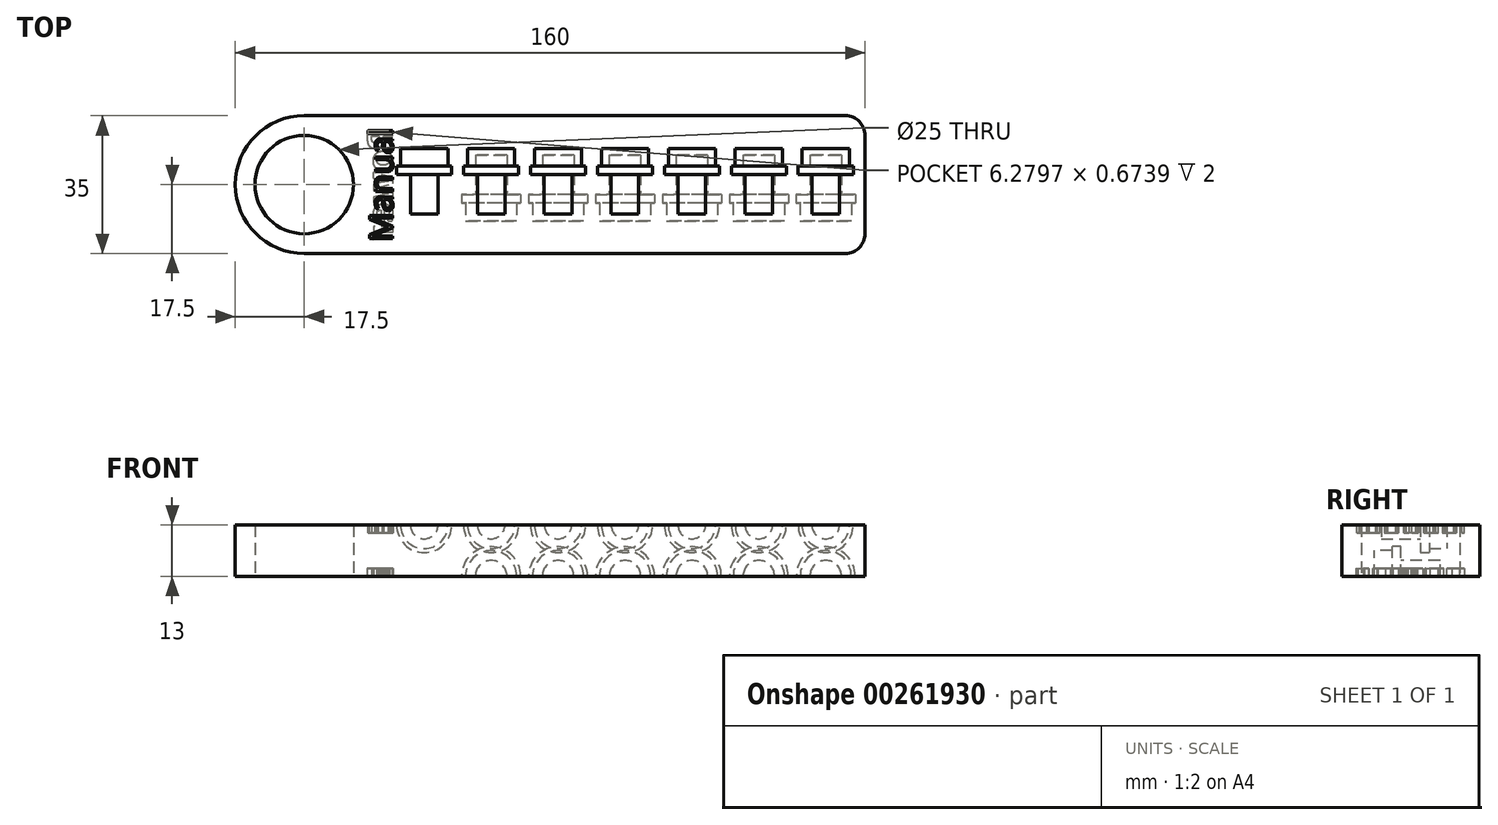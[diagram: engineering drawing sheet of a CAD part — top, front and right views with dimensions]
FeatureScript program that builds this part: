
annotation { "Feature Type Name" : "Feature", "Feature Type Description" : "" }
export const myFeature = defineFeature(function(context is Context, id is Id, definition is map)
    precondition{}
    {
        {
            var Q0;
            Q0=qCreatedBy(makeId("Top.planeOp"),FACE);
            var sketch = newSketch(context, id + "F0", { "sketchPlane" : qUnion([Q0])});
            skLineSegment(sketch, "E0.bottom", {"start": v(17.5, 0) * mm, "end": v(155, 0) * mm});
            skLineSegment(sketch, "E0.top", {"start": v(17.5, 35) * mm, "end": v(155, 35) * mm});
            skLineSegment(sketch, "E0.left", {"start": v(0, 17.5) * mm, "end": v(0, 17.5) * mm});
            skLineSegment(sketch, "E0.right", {"start": v(160, 5) * mm, "end": v(160, 30) * mm});
            skLineSegment(sketch, "E1.bottom", {"start": v(0, 0) * mm, "end": v(17.5, 0) * mm, "construction": true});
            skLineSegment(sketch, "E1.top", {"start": v(0, 17.5) * mm, "end": v(17.5, 17.5) * mm, "construction": true});
            skLineSegment(sketch, "E1.left", {"start": v(0, 0) * mm, "end": v(0, 17.5) * mm, "construction": true});
            skLineSegment(sketch, "E1.right", {"start": v(17.5, 0) * mm, "end": v(17.5, 17.5) * mm, "construction": true});
            skCircle(sketch, "E2", {"center": v(17.5, 17.5) * mm, "radius": 12.5 * mm});
            skPoint(sketch, "E3.visualSharp", {"position": v(0, 35) * mm});
            skArc(sketch, "E3.filletArc", {"start": v(17.5, 35) * mm, "mid": v(5.13, 29.87) * mm, "end": v(0, 17.5) * mm});
            skPoint(sketch, "E4.visualSharp", {"position": v(0, 0) * mm});
            skArc(sketch, "E4.filletArc", {"start": v(0, 17.5) * mm, "mid": v(5.13, 5.13) * mm, "end": v(17.5, 0) * mm});
            skPoint(sketch, "E5.visualSharp", {"position": v(160, 35) * mm});
            skArc(sketch, "E5.filletArc", {"start": v(160, 30) * mm, "mid": v(158.54, 33.54) * mm, "end": v(155, 35) * mm});
            skPoint(sketch, "E6.visualSharp", {"position": v(160, 0) * mm});
            skArc(sketch, "E6.filletArc", {"start": v(155, 0) * mm, "mid": v(158.54, 1.46) * mm, "end": v(160, 5) * mm});
            skSolve(sketch);
        }
        {
            var Q0;
            Q0=makeQuery(id+"F0.imprint","IMPRINT",FACE,{"disambiguationData":[TD([[makeQuery(id+"F0.imprint","IMPRINT",EDGE,{"derivedFrom":sQuery(id+"F0.wireOp",EDGE,"E0.bottom")}),1.0]])]});
            extrude(context, id + "F1", {"entities" : qUnion([Q0]), "depth" : 13 * mm});
        }
        {
            var Q0;
            Q0=makeQuery(id+"F1.opExtrude","CAP_FACE",FACE,{"disambiguationData":[OSD([sQuery(id+"F0.wireOp",EDGE,"E0.bottom"),sQuery(id+"F0.wireOp",EDGE,"E0.top"),sQuery(id+"F0.wireOp",EDGE,"E0.left"),sQuery(id+"F0.wireOp",EDGE,"E0.right"),sQuery(id+"F0.wireOp",EDGE,"E2"),sQuery(id+"F0.wireOp",EDGE,"E3.filletArc"),sQuery(id+"F0.wireOp",EDGE,"E4.filletArc"),sQuery(id+"F0.wireOp",EDGE,"E5.filletArc"),sQuery(id+"F0.wireOp",EDGE,"E6.filletArc")])],"isStart":false});
            var sketch = newSketch(context, id + "F2", { "sketchPlane" : qUnion([Q0])});
            skLineSegment(sketch, "E7.bottom", {"start": v(0, 0) * mm, "end": v(48, 0) * mm, "construction": true});
            skLineSegment(sketch, "E7.top", {"start": v(0, 10) * mm, "end": v(48, 10) * mm, "construction": true});
            skLineSegment(sketch, "E7.left", {"start": v(0, 0) * mm, "end": v(0, 10) * mm, "construction": true});
            skLineSegment(sketch, "E7.right", {"start": v(48, 0) * mm, "end": v(48, 10) * mm, "construction": true});
            skLineSegment(sketch, "E8", {"start": v(48, 10) * mm, "end": v(65, 10) * mm, "construction": true});
            skLineSegment(sketch, "E9", {"start": v(65, 10) * mm, "end": v(82, 10) * mm, "construction": true});
            skLineSegment(sketch, "E10", {"start": v(82, 10) * mm, "end": v(99, 10) * mm, "construction": true});
            skLineSegment(sketch, "E11", {"start": v(99, 10) * mm, "end": v(116, 10) * mm, "construction": true});
            skLineSegment(sketch, "E12", {"start": v(116, 10) * mm, "end": v(133, 10) * mm, "construction": true});
            skLineSegment(sketch, "E13", {"start": v(133, 10) * mm, "end": v(150, 10) * mm, "construction": true});
            skLineSegment(sketch, "E14.bottom", {"start": v(48, 10) * mm, "end": v(51.5, 10) * mm});
            skLineSegment(sketch, "E14.left", {"start": v(48, 10) * mm, "end": v(48, 20) * mm});
            skLineSegment(sketch, "E14.right", {"start": v(51.5, 10) * mm, "end": v(51.5, 20) * mm});
            skLineSegment(sketch, "E15.bottom", {"start": v(65, 10) * mm, "end": v(68.5, 10) * mm});
            skLineSegment(sketch, "E15.left", {"start": v(65, 10) * mm, "end": v(65, 20) * mm});
            skLineSegment(sketch, "E15.right", {"start": v(68.5, 10) * mm, "end": v(68.5, 20) * mm});
            skLineSegment(sketch, "E16.bottom", {"start": v(82, 10) * mm, "end": v(85.5, 10) * mm});
            skLineSegment(sketch, "E16.left", {"start": v(82, 10) * mm, "end": v(82, 20) * mm});
            skLineSegment(sketch, "E16.right", {"start": v(85.5, 10) * mm, "end": v(85.5, 20) * mm});
            skLineSegment(sketch, "E17.bottom", {"start": v(99, 10) * mm, "end": v(102.5, 10) * mm});
            skLineSegment(sketch, "E17.left", {"start": v(99, 10) * mm, "end": v(99, 20) * mm});
            skLineSegment(sketch, "E17.right", {"start": v(102.5, 10) * mm, "end": v(102.5, 20) * mm});
            skLineSegment(sketch, "E18.bottom", {"start": v(116, 10) * mm, "end": v(119.5, 10) * mm});
            skLineSegment(sketch, "E18.left", {"start": v(116, 10) * mm, "end": v(116, 20) * mm});
            skLineSegment(sketch, "E18.right", {"start": v(119.5, 10) * mm, "end": v(119.5, 20) * mm});
            skLineSegment(sketch, "E19.bottom", {"start": v(133, 10) * mm, "end": v(136.5, 10) * mm});
            skLineSegment(sketch, "E19.left", {"start": v(133, 10) * mm, "end": v(133, 20) * mm});
            skLineSegment(sketch, "E19.right", {"start": v(136.5, 10) * mm, "end": v(136.5, 20) * mm});
            skLineSegment(sketch, "E20.bottom", {"start": v(150, 10) * mm, "end": v(153.5, 10) * mm});
            skLineSegment(sketch, "E20.left", {"start": v(150, 10) * mm, "end": v(150, 20) * mm});
            skLineSegment(sketch, "E20.right", {"start": v(153.5, 10) * mm, "end": v(153.5, 20) * mm});
            skLineSegment(sketch, "E21.bottom", {"start": v(153.5, 20) * mm, "end": v(157, 20) * mm});
            skLineSegment(sketch, "E21.top", {"start": v(156, 22.2) * mm, "end": v(157, 22.2) * mm});
            skLineSegment(sketch, "E21.left", {"start": v(150, 20) * mm, "end": v(150, 22.2) * mm});
            skLineSegment(sketch, "E21.right", {"start": v(157, 20) * mm, "end": v(157, 22.2) * mm});
            skLineSegment(sketch, "E22.bottom", {"start": v(136.5, 20) * mm, "end": v(140, 20) * mm});
            skLineSegment(sketch, "E22.top", {"start": v(139, 22.2) * mm, "end": v(140, 22.2) * mm});
            skLineSegment(sketch, "E22.left", {"start": v(133, 20) * mm, "end": v(133, 22.2) * mm});
            skLineSegment(sketch, "E22.right", {"start": v(140, 20) * mm, "end": v(140, 22.2) * mm});
            skLineSegment(sketch, "E23.bottom", {"start": v(119.5, 20) * mm, "end": v(123, 20) * mm});
            skLineSegment(sketch, "E23.top", {"start": v(122, 22.2) * mm, "end": v(123, 22.2) * mm});
            skLineSegment(sketch, "E23.left", {"start": v(116, 20) * mm, "end": v(116, 22.2) * mm});
            skLineSegment(sketch, "E23.right", {"start": v(123, 20) * mm, "end": v(123, 22.2) * mm});
            skLineSegment(sketch, "E24.bottom", {"start": v(102.5, 20) * mm, "end": v(106, 20) * mm});
            skLineSegment(sketch, "E24.top", {"start": v(105, 22.2) * mm, "end": v(106, 22.2) * mm});
            skLineSegment(sketch, "E24.left", {"start": v(99, 20) * mm, "end": v(99, 22.2) * mm});
            skLineSegment(sketch, "E24.right", {"start": v(106, 20) * mm, "end": v(106, 22.2) * mm});
            skLineSegment(sketch, "E25.bottom", {"start": v(85.5, 20) * mm, "end": v(89, 20) * mm});
            skLineSegment(sketch, "E25.top", {"start": v(88, 22.2) * mm, "end": v(89, 22.2) * mm});
            skLineSegment(sketch, "E25.left", {"start": v(82, 20) * mm, "end": v(82, 22.2) * mm});
            skLineSegment(sketch, "E25.right", {"start": v(89, 20) * mm, "end": v(89, 22.2) * mm});
            skLineSegment(sketch, "E26.bottom", {"start": v(68.5, 20) * mm, "end": v(72, 20) * mm});
            skLineSegment(sketch, "E26.top", {"start": v(71, 22.2) * mm, "end": v(72, 22.2) * mm});
            skLineSegment(sketch, "E26.left", {"start": v(65, 20) * mm, "end": v(65, 22.2) * mm});
            skLineSegment(sketch, "E26.right", {"start": v(72, 20) * mm, "end": v(72, 22.2) * mm});
            skLineSegment(sketch, "E27.bottom", {"start": v(51.5, 20) * mm, "end": v(55, 20) * mm});
            skLineSegment(sketch, "E27.top", {"start": v(54, 22.2) * mm, "end": v(55, 22.2) * mm});
            skLineSegment(sketch, "E27.left", {"start": v(48, 20) * mm, "end": v(48, 22.2) * mm});
            skLineSegment(sketch, "E27.right", {"start": v(55, 20) * mm, "end": v(55, 22.2) * mm});
            skLineSegment(sketch, "E28.top", {"start": v(48, 26.7) * mm, "end": v(54, 26.7) * mm});
            skLineSegment(sketch, "E28.left", {"start": v(48, 22.2) * mm, "end": v(48, 26.7) * mm});
            skLineSegment(sketch, "E28.right", {"start": v(54, 22.2) * mm, "end": v(54, 26.7) * mm});
            skLineSegment(sketch, "E29.top", {"start": v(65, 26.7) * mm, "end": v(71, 26.7) * mm});
            skLineSegment(sketch, "E29.left", {"start": v(65, 22.2) * mm, "end": v(65, 26.7) * mm});
            skLineSegment(sketch, "E29.right", {"start": v(71, 22.2) * mm, "end": v(71, 26.7) * mm});
            skLineSegment(sketch, "E30.top", {"start": v(82, 26.7) * mm, "end": v(88, 26.7) * mm});
            skLineSegment(sketch, "E30.left", {"start": v(82, 22.2) * mm, "end": v(82, 26.7) * mm});
            skLineSegment(sketch, "E30.right", {"start": v(88, 22.2) * mm, "end": v(88, 26.7) * mm});
            skLineSegment(sketch, "E31.top", {"start": v(99, 26.7) * mm, "end": v(105, 26.7) * mm});
            skLineSegment(sketch, "E31.left", {"start": v(99, 22.2) * mm, "end": v(99, 26.7) * mm});
            skLineSegment(sketch, "E31.right", {"start": v(105, 22.2) * mm, "end": v(105, 26.7) * mm});
            skLineSegment(sketch, "E32.top", {"start": v(116, 26.7) * mm, "end": v(122, 26.7) * mm});
            skLineSegment(sketch, "E32.left", {"start": v(116, 22.2) * mm, "end": v(116, 26.7) * mm});
            skLineSegment(sketch, "E32.right", {"start": v(122, 22.2) * mm, "end": v(122, 26.7) * mm});
            skLineSegment(sketch, "E33.top", {"start": v(133, 26.7) * mm, "end": v(139, 26.7) * mm});
            skLineSegment(sketch, "E33.left", {"start": v(133, 22.2) * mm, "end": v(133, 26.7) * mm});
            skLineSegment(sketch, "E33.right", {"start": v(139, 22.2) * mm, "end": v(139, 26.7) * mm});
            skLineSegment(sketch, "E34.top", {"start": v(150, 26.7) * mm, "end": v(156, 26.7) * mm});
            skLineSegment(sketch, "E34.left", {"start": v(150, 22.2) * mm, "end": v(150, 26.7) * mm});
            skLineSegment(sketch, "E34.right", {"start": v(156, 22.2) * mm, "end": v(156, 26.7) * mm});
            skSolve(sketch);
        }
        {
            var Q0;
            Q0=makeQuery(id+"F2.imprint","IMPRINT",FACE,{"disambiguationData":[TD([[makeQuery(id+"F2.imprint","IMPRINT",EDGE,{"derivedFrom":sQuery(id+"F2.wireOp",EDGE,"E14.bottom")}),1.0]])]});
            var Q1;
            Q1=sQuery(id+"F2.wireOp",EDGE,"E14.left");
            revolve(context, id + "F3", {"operationType" : NewBodyOperationType.REMOVE, "entities" : qUnion([Q0]), "axis" : qUnion([Q1]), "revolveType" : RevolveType.FULL, "oppositeDirection" : true});
        }
        {
            var Q0;
            Q0=makeQuery(id+"F2.imprint","IMPRINT",FACE,{"disambiguationData":[TD([[makeQuery(id+"F2.imprint","IMPRINT",EDGE,{"derivedFrom":sQuery(id+"F2.wireOp",EDGE,"E15.bottom")}),1.0]])]});
            var Q1;
            Q1=sQuery(id+"F2.wireOp",EDGE,"E15.left");
            revolve(context, id + "F4", {"operationType" : NewBodyOperationType.REMOVE, "entities" : qUnion([Q0]), "axis" : qUnion([Q1]), "revolveType" : RevolveType.FULL, "oppositeDirection" : true});
        }
        {
            var Q0;
            Q0=makeQuery(id+"F2.imprint","IMPRINT",FACE,{"disambiguationData":[TD([[makeQuery(id+"F2.imprint","IMPRINT",EDGE,{"derivedFrom":sQuery(id+"F2.wireOp",EDGE,"E16.bottom")}),1.0]])]});
            var Q1;
            Q1=sQuery(id+"F2.wireOp",EDGE,"E16.left");
            revolve(context, id + "F5", {"operationType" : NewBodyOperationType.REMOVE, "entities" : qUnion([Q0]), "axis" : qUnion([Q1]), "revolveType" : RevolveType.FULL, "oppositeDirection" : true});
        }
        {
            var Q0;
            Q0=makeQuery(id+"F2.imprint","IMPRINT",FACE,{"disambiguationData":[TD([[makeQuery(id+"F2.imprint","IMPRINT",EDGE,{"derivedFrom":sQuery(id+"F2.wireOp",EDGE,"E17.bottom")}),1.0]])]});
            var Q1;
            Q1=sQuery(id+"F2.wireOp",EDGE,"E17.left");
            revolve(context, id + "F6", {"operationType" : NewBodyOperationType.REMOVE, "entities" : qUnion([Q0]), "axis" : qUnion([Q1]), "revolveType" : RevolveType.FULL, "oppositeDirection" : true});
        }
        {
            var Q0;
            Q0=makeQuery(id+"F2.imprint","IMPRINT",FACE,{"disambiguationData":[TD([[makeQuery(id+"F2.imprint","IMPRINT",EDGE,{"derivedFrom":sQuery(id+"F2.wireOp",EDGE,"E18.bottom")}),1.0]])]});
            var Q1;
            Q1=sQuery(id+"F2.wireOp",EDGE,"E18.left");
            revolve(context, id + "F7", {"operationType" : NewBodyOperationType.REMOVE, "entities" : qUnion([Q0]), "axis" : qUnion([Q1]), "revolveType" : RevolveType.FULL, "oppositeDirection" : true});
        }
        {
            var Q0;
            Q0=makeQuery(id+"F2.imprint","IMPRINT",FACE,{"disambiguationData":[TD([[makeQuery(id+"F2.imprint","IMPRINT",EDGE,{"derivedFrom":sQuery(id+"F2.wireOp",EDGE,"E19.bottom")}),1.0]])]});
            var Q1;
            Q1=sQuery(id+"F2.wireOp",EDGE,"E19.left");
            revolve(context, id + "F8", {"operationType" : NewBodyOperationType.REMOVE, "entities" : qUnion([Q0]), "axis" : qUnion([Q1]), "revolveType" : RevolveType.FULL, "oppositeDirection" : true});
        }
        {
            var Q0;
            Q0=makeQuery(id+"F2.imprint","IMPRINT",FACE,{"disambiguationData":[TD([[makeQuery(id+"F2.imprint","IMPRINT",EDGE,{"derivedFrom":sQuery(id+"F2.wireOp",EDGE,"E20.bottom")}),1.0]])]});
            var Q1;
            Q1=sQuery(id+"F2.wireOp",EDGE,"E20.left");
            revolve(context, id + "F9", {"operationType" : NewBodyOperationType.REMOVE, "entities" : qUnion([Q0]), "axis" : qUnion([Q1]), "revolveType" : RevolveType.FULL, "oppositeDirection" : true});
        }
        {
            var Q0;
            Q0=makeQuery(id+"F1.opExtrude","CAP_FACE",FACE,{"disambiguationData":[OSD([sQuery(id+"F0.wireOp",EDGE,"E0.bottom"),sQuery(id+"F0.wireOp",EDGE,"E0.top"),sQuery(id+"F0.wireOp",EDGE,"E0.left"),sQuery(id+"F0.wireOp",EDGE,"E0.right"),sQuery(id+"F0.wireOp",EDGE,"E2"),sQuery(id+"F0.wireOp",EDGE,"E3.filletArc"),sQuery(id+"F0.wireOp",EDGE,"E4.filletArc"),sQuery(id+"F0.wireOp",EDGE,"E5.filletArc"),sQuery(id+"F0.wireOp",EDGE,"E6.filletArc")])],"isStart":false});
            var sketch = newSketch(context, id + "F10", { "sketchPlane" : qUnion([Q0])});
            skText(sketch, "E35", { "text": "Manual", "fontName": "OpenSans-Regular.ttf"});
            skLineSegment(sketch, "E36.bottom", {"start": v(0, 0) * mm, "end": v(40, 0) * mm, "construction": true});
            skLineSegment(sketch, "E36.top", {"start": v(0, 3) * mm, "end": v(40, 3) * mm, "construction": true});
            skLineSegment(sketch, "E36.left", {"start": v(0, 0) * mm, "end": v(0, 3) * mm, "construction": true});
            skLineSegment(sketch, "E36.right", {"start": v(40, 0) * mm, "end": v(40, 3) * mm, "construction": true});
            skLineSegment(sketch, "E37.top", {"start": v(0, 32) * mm, "end": v(40, 32) * mm, "construction": true});
            skLineSegment(sketch, "E37.left", {"start": v(0, 0) * mm, "end": v(0, 32) * mm, "construction": true});
            skLineSegment(sketch, "E37.right", {"start": v(40, 0) * mm, "end": v(40, 32) * mm, "construction": true});
            const initialGuessF10  = {"E35": [0.04, 0.003, 0.0006, 1, 0.00595]};
            skSetInitialGuess(sketch, initialGuessF10);
            skSolve(sketch);
        }
        {
            var Q0;
            Q0 = qSketchRegion(id + "F10", true);
            extrude(context, id + "F11", {"entities" : qUnion([Q0]), "operationType" : NewBodyOperationType.REMOVE, "oppositeDirection" : true, "depth" : 2 * mm});
        }
        {
            var Q0;
            Q0=makeQuery(id+"F1.opExtrude","CAP_FACE",FACE,{"disambiguationData":[OSD([sQuery(id+"F0.wireOp",EDGE,"E0.bottom"),sQuery(id+"F0.wireOp",EDGE,"E0.top"),sQuery(id+"F0.wireOp",EDGE,"E0.left"),sQuery(id+"F0.wireOp",EDGE,"E0.right"),sQuery(id+"F0.wireOp",EDGE,"E2"),sQuery(id+"F0.wireOp",EDGE,"E3.filletArc"),sQuery(id+"F0.wireOp",EDGE,"E4.filletArc"),sQuery(id+"F0.wireOp",EDGE,"E5.filletArc"),sQuery(id+"F0.wireOp",EDGE,"E6.filletArc")])],"isStart":true});
            var sketch = newSketch(context, id + "F12", { "sketchPlane" : qUnion([Q0])});
            skLineSegment(sketch, "E38.bottom", {"start": v(0, 0) * mm, "end": v(65, 0) * mm, "construction": true});
            skLineSegment(sketch, "E38.top", {"start": v(0, -25) * mm, "end": v(65, -25) * mm, "construction": true});
            skLineSegment(sketch, "E38.left", {"start": v(0, 0) * mm, "end": v(0, -25) * mm, "construction": true});
            skLineSegment(sketch, "E38.right", {"start": v(65, 0) * mm, "end": v(65, -25) * mm, "construction": true});
            skLineSegment(sketch, "E39", {"start": v(65, -25) * mm, "end": v(82, -25) * mm, "construction": true});
            skLineSegment(sketch, "E40", {"start": v(82, -25) * mm, "end": v(99, -25) * mm, "construction": true});
            skPoint(sketch, "E40.endSnap0", {"position": v(73.5, -25) * mm});
            skLineSegment(sketch, "E41", {"start": v(99, -25) * mm, "end": v(116, -25) * mm, "construction": true});
            skLineSegment(sketch, "E42", {"start": v(116, -25) * mm, "end": v(133, -25) * mm, "construction": true});
            skLineSegment(sketch, "E43", {"start": v(133, -25) * mm, "end": v(150, -25) * mm, "construction": true});
            skLineSegment(sketch, "E44.bottom", {"start": v(65, -25) * mm, "end": v(69, -25) * mm});
            skLineSegment(sketch, "E44.left", {"start": v(65, -25) * mm, "end": v(65, -15) * mm});
            skLineSegment(sketch, "E44.right", {"start": v(69, -25) * mm, "end": v(69, -15) * mm});
            skLineSegment(sketch, "E45.bottom", {"start": v(82, -25) * mm, "end": v(86, -25) * mm});
            skLineSegment(sketch, "E45.left", {"start": v(82, -25) * mm, "end": v(82, -15) * mm});
            skLineSegment(sketch, "E45.right", {"start": v(86, -25) * mm, "end": v(86, -15) * mm});
            skLineSegment(sketch, "E46.bottom", {"start": v(99, -25) * mm, "end": v(103, -25) * mm});
            skLineSegment(sketch, "E46.left", {"start": v(99, -25) * mm, "end": v(99, -15) * mm});
            skLineSegment(sketch, "E46.right", {"start": v(103, -25) * mm, "end": v(103, -15) * mm});
            skLineSegment(sketch, "E47.bottom", {"start": v(116, -25) * mm, "end": v(120, -25) * mm});
            skLineSegment(sketch, "E47.left", {"start": v(116, -25) * mm, "end": v(116, -15) * mm});
            skLineSegment(sketch, "E47.right", {"start": v(120, -25) * mm, "end": v(120, -15) * mm});
            skLineSegment(sketch, "E48.bottom", {"start": v(133, -25) * mm, "end": v(137, -25) * mm});
            skLineSegment(sketch, "E48.left", {"start": v(133, -25) * mm, "end": v(133, -15) * mm});
            skLineSegment(sketch, "E48.right", {"start": v(137, -25) * mm, "end": v(137, -15) * mm});
            skLineSegment(sketch, "E49.bottom", {"start": v(150, -25) * mm, "end": v(154, -25) * mm});
            skLineSegment(sketch, "E49.left", {"start": v(150, -25) * mm, "end": v(150, -15) * mm});
            skLineSegment(sketch, "E49.right", {"start": v(154, -25) * mm, "end": v(154, -15) * mm});
            skLineSegment(sketch, "E50.bottom", {"start": v(154, -15) * mm, "end": v(157.5, -15) * mm});
            skLineSegment(sketch, "E50.top", {"start": v(156.5, -12.8) * mm, "end": v(157.5, -12.8) * mm});
            skLineSegment(sketch, "E50.left", {"start": v(150, -15) * mm, "end": v(150, -12.8) * mm});
            skLineSegment(sketch, "E50.right", {"start": v(157.5, -15) * mm, "end": v(157.5, -12.8) * mm});
            skLineSegment(sketch, "E51.bottom", {"start": v(137, -15) * mm, "end": v(140.5, -15) * mm});
            skLineSegment(sketch, "E51.top", {"start": v(139.5, -12.8) * mm, "end": v(140.5, -12.8) * mm});
            skLineSegment(sketch, "E51.left", {"start": v(133, -15) * mm, "end": v(133, -12.8) * mm});
            skLineSegment(sketch, "E51.right", {"start": v(140.5, -15) * mm, "end": v(140.5, -12.8) * mm});
            skLineSegment(sketch, "E52.bottom", {"start": v(120, -15) * mm, "end": v(123.5, -15) * mm});
            skLineSegment(sketch, "E52.top", {"start": v(122.5, -12.8) * mm, "end": v(123.5, -12.8) * mm});
            skLineSegment(sketch, "E52.left", {"start": v(116, -15) * mm, "end": v(116, -12.8) * mm});
            skLineSegment(sketch, "E52.right", {"start": v(123.5, -15) * mm, "end": v(123.5, -12.8) * mm});
            skLineSegment(sketch, "E53.bottom", {"start": v(103, -15) * mm, "end": v(106.5, -15) * mm});
            skLineSegment(sketch, "E53.top", {"start": v(105.5, -12.8) * mm, "end": v(106.5, -12.8) * mm});
            skLineSegment(sketch, "E53.left", {"start": v(99, -15) * mm, "end": v(99, -12.8) * mm});
            skLineSegment(sketch, "E53.right", {"start": v(106.5, -15) * mm, "end": v(106.5, -12.8) * mm});
            skLineSegment(sketch, "E54.bottom", {"start": v(86, -15) * mm, "end": v(89.5, -15) * mm});
            skLineSegment(sketch, "E54.top", {"start": v(88.5, -12.8) * mm, "end": v(89.5, -12.8) * mm});
            skLineSegment(sketch, "E54.left", {"start": v(82, -15) * mm, "end": v(82, -12.8) * mm});
            skLineSegment(sketch, "E54.right", {"start": v(89.5, -15) * mm, "end": v(89.5, -12.8) * mm});
            skLineSegment(sketch, "E55.bottom", {"start": v(69, -15) * mm, "end": v(72.5, -15) * mm});
            skLineSegment(sketch, "E55.top", {"start": v(71.5, -12.8) * mm, "end": v(72.5, -12.8) * mm});
            skLineSegment(sketch, "E55.left", {"start": v(65, -15) * mm, "end": v(65, -12.8) * mm});
            skLineSegment(sketch, "E55.right", {"start": v(72.5, -15) * mm, "end": v(72.5, -12.8) * mm});
            skLineSegment(sketch, "E56.top", {"start": v(65, -8.3) * mm, "end": v(71.5, -8.3) * mm});
            skLineSegment(sketch, "E56.left", {"start": v(65, -12.8) * mm, "end": v(65, -8.3) * mm});
            skLineSegment(sketch, "E56.right", {"start": v(71.5, -12.8) * mm, "end": v(71.5, -8.3) * mm});
            skLineSegment(sketch, "E57.top", {"start": v(82, -8.3) * mm, "end": v(88.5, -8.3) * mm});
            skLineSegment(sketch, "E57.left", {"start": v(82, -12.8) * mm, "end": v(82, -8.3) * mm});
            skLineSegment(sketch, "E57.right", {"start": v(88.5, -12.8) * mm, "end": v(88.5, -8.3) * mm});
            skLineSegment(sketch, "E58.top", {"start": v(99, -8.3) * mm, "end": v(105.5, -8.3) * mm});
            skLineSegment(sketch, "E58.left", {"start": v(99, -12.8) * mm, "end": v(99, -8.3) * mm});
            skLineSegment(sketch, "E58.right", {"start": v(105.5, -12.8) * mm, "end": v(105.5, -8.3) * mm});
            skLineSegment(sketch, "E59.top", {"start": v(116, -8.3) * mm, "end": v(122.5, -8.3) * mm});
            skLineSegment(sketch, "E59.left", {"start": v(116, -12.8) * mm, "end": v(116, -8.3) * mm});
            skLineSegment(sketch, "E59.right", {"start": v(122.5, -12.8) * mm, "end": v(122.5, -8.3) * mm});
            skLineSegment(sketch, "E60.top", {"start": v(133, -8.3) * mm, "end": v(139.5, -8.3) * mm});
            skLineSegment(sketch, "E60.left", {"start": v(133, -12.8) * mm, "end": v(133, -8.3) * mm});
            skLineSegment(sketch, "E60.right", {"start": v(139.5, -12.8) * mm, "end": v(139.5, -8.3) * mm});
            skLineSegment(sketch, "E61.top", {"start": v(150, -8.3) * mm, "end": v(156.5, -8.3) * mm});
            skLineSegment(sketch, "E61.left", {"start": v(150, -12.8) * mm, "end": v(150, -8.3) * mm});
            skLineSegment(sketch, "E61.right", {"start": v(156.5, -12.8) * mm, "end": v(156.5, -8.3) * mm});
            skSolve(sketch);
        }
        {
            var Q0;
            Q0=makeQuery(id+"F12.imprint","IMPRINT",FACE,{"disambiguationData":[TD([[makeQuery(id+"F12.imprint","IMPRINT",EDGE,{"derivedFrom":sQuery(id+"F12.wireOp",EDGE,"E44.bottom")}),1.0]])]});
            var Q1;
            Q1=sQuery(id+"F12.wireOp",EDGE,"E44.left");
            revolve(context, id + "F13", {"operationType" : NewBodyOperationType.REMOVE, "entities" : qUnion([Q0]), "axis" : qUnion([Q1]), "revolveType" : RevolveType.FULL, "oppositeDirection" : true});
        }
        {
            var Q0;
            Q0=makeQuery(id+"F12.imprint","IMPRINT",FACE,{"disambiguationData":[TD([[makeQuery(id+"F12.imprint","IMPRINT",EDGE,{"derivedFrom":sQuery(id+"F12.wireOp",EDGE,"E45.bottom")}),1.0]])]});
            var Q1;
            Q1=sQuery(id+"F12.wireOp",EDGE,"E45.left");
            revolve(context, id + "F14", {"operationType" : NewBodyOperationType.REMOVE, "entities" : qUnion([Q0]), "axis" : qUnion([Q1]), "revolveType" : RevolveType.FULL, "oppositeDirection" : true});
        }
        {
            var Q0;
            Q0=makeQuery(id+"F12.imprint","IMPRINT",FACE,{"disambiguationData":[TD([[makeQuery(id+"F12.imprint","IMPRINT",EDGE,{"derivedFrom":sQuery(id+"F12.wireOp",EDGE,"E46.bottom")}),1.0]])]});
            var Q1;
            Q1=sQuery(id+"F12.wireOp",EDGE,"E46.left");
            revolve(context, id + "F15", {"operationType" : NewBodyOperationType.REMOVE, "entities" : qUnion([Q0]), "axis" : qUnion([Q1]), "revolveType" : RevolveType.FULL, "oppositeDirection" : true});
        }
        {
            var Q0;
            Q0=makeQuery(id+"F12.imprint","IMPRINT",FACE,{"disambiguationData":[TD([[makeQuery(id+"F12.imprint","IMPRINT",EDGE,{"derivedFrom":sQuery(id+"F12.wireOp",EDGE,"E47.bottom")}),1.0]])]});
            var Q1;
            Q1=sQuery(id+"F12.wireOp",EDGE,"E47.left");
            revolve(context, id + "F16", {"operationType" : NewBodyOperationType.REMOVE, "entities" : qUnion([Q0]), "axis" : qUnion([Q1]), "revolveType" : RevolveType.FULL, "oppositeDirection" : true});
        }
        {
            var Q0;
            Q0=makeQuery(id+"F12.imprint","IMPRINT",FACE,{"disambiguationData":[TD([[makeQuery(id+"F12.imprint","IMPRINT",EDGE,{"derivedFrom":sQuery(id+"F12.wireOp",EDGE,"E48.bottom")}),1.0]])]});
            var Q1;
            Q1=sQuery(id+"F12.wireOp",EDGE,"E48.left");
            revolve(context, id + "F17", {"operationType" : NewBodyOperationType.REMOVE, "entities" : qUnion([Q0]), "axis" : qUnion([Q1]), "revolveType" : RevolveType.FULL, "oppositeDirection" : true});
        }
        {
            var Q0;
            Q0=makeQuery(id+"F12.imprint","IMPRINT",FACE,{"disambiguationData":[TD([[makeQuery(id+"F12.imprint","IMPRINT",EDGE,{"derivedFrom":sQuery(id+"F12.wireOp",EDGE,"E49.bottom")}),1.0]])]});
            var Q1;
            Q1=sQuery(id+"F12.wireOp",EDGE,"E49.left");
            revolve(context, id + "F18", {"operationType" : NewBodyOperationType.REMOVE, "entities" : qUnion([Q0]), "axis" : qUnion([Q1]), "revolveType" : RevolveType.FULL, "oppositeDirection" : true});
        }
        {
            var Q0;
            Q0=makeQuery(id+"F12.imprint","IMPRINT",FACE,{"disambiguationData":[TD([[makeQuery(id+"F12.imprint","IMPRINT",EDGE,{"derivedFrom":sQuery(id+"F12.wireOp",EDGE,"E44.bottom")}),-1.0]])]});
            var sketch = newSketch(context, id + "F19", { "sketchPlane" : qUnion([Q0])});
            skLineSegment(sketch, "E62.bottom", {"start": v(0, 0) * mm, "end": v(40, 0) * mm, "construction": true});
            skLineSegment(sketch, "E62.top", {"start": v(0, -32) * mm, "end": v(40, -32) * mm, "construction": true});
            skLineSegment(sketch, "E62.left", {"start": v(0, 0) * mm, "end": v(0, -32) * mm, "construction": true});
            skLineSegment(sketch, "E62.right", {"start": v(40, 0) * mm, "end": v(40, -32) * mm, "construction": true});
            skLineSegment(sketch, "E63.top", {"start": v(0, -3) * mm, "end": v(40, -3) * mm, "construction": true});
            skLineSegment(sketch, "E63.left", {"start": v(0, 0) * mm, "end": v(0, -3) * mm, "construction": true});
            skLineSegment(sketch, "E63.right", {"start": v(40, 0) * mm, "end": v(40, -3) * mm, "construction": true});
            skText(sketch, "E64", { "text": "Power", "fontName": "OpenSans-Bold.ttf"});
            const initialGuessF19  = {"E64": [0.04, -0.032, 0.00261, 1, 0.00654]};
            skSetInitialGuess(sketch, initialGuessF19);
            skSolve(sketch);
        }
        {
            var Q0;
            Q0 = qSketchRegion(id + "F19", true);
            extrude(context, id + "F20", {"entities" : qUnion([Q0]), "operationType" : NewBodyOperationType.REMOVE, "oppositeDirection" : true, "depth" : 2 * mm});
        }
    });
